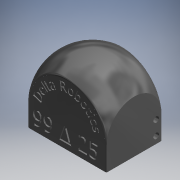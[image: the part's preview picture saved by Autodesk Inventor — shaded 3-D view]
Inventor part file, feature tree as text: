
AUTODESK INVENTOR PART (.ipt)
format: ipt  version: 2019 (Build 230136000, 136)  size: 742,912 bytes
history: native  units: mm (DEFAULTED — no unit token found)
features: sketch x11, extrude x10, plane x5, mirror x3, revolve x1, fillet x1
ambient origin geometry x8: Origin, YZ Plane, XZ Plane, XY Plane, X Axis, Y Axis, Z Axis, Center Point
bodies: Solid1 (feature_tree)
feature tree (31):
  extrude  "Extrusion1"  Depth=88.9mm
  extrude  "Extrusion2"  Depth=25.4mm
  extrude  "Extrusion3"  Depth=3.175mm TaperAngle=0.0deg
  plane  "Work Plane1"
  mirror  "Mirror1"
  plane  "Work Plane2"
  revolve  "Revolution1"  [1 undecoded]
  extrude  "Extrusion4"  Depth=44.45mm
  plane  "Work Plane3"
  mirror  "Mirror2"
  fillet  "Fillet1"  Radius=44.45mm
  sketch  "Sketch7"  dims[d14=180.0deg d15=25.4mm d16=0.0mm]
  extrude  "Extrusion5"  Depth=25.4mm TaperAngle=0.0deg
  extrude  "Extrusion6"  Depth=3.175mm
  plane  "Work Plane4"
  extrude  "Extrusion7"  Depth=8.001mm
  plane  "Work Plane5"
  mirror  "Mirror3"
  extrude  "Extrusion8"  Depth=6.35mm
  extrude  "Extrusion9"  Depth=3.048mm
  extrude  "Extrusion10"  Depth=3.175mm TaperAngle=0.0deg
  sketch  "Sketch1"  dims[d0=82.55mm d1=88.9mm]
  sketch  "Sketch2"  dims[d2=25.4mm d3=25.4mm]
  sketch  "Sketch3"  dims[d4=59.69mm d5=0.0mm d6=3.175mm d7=0.0mm]
  sketch  "Sketch5"  dims[d8=12.7mm d9=25.4mm]
  sketch  "Sketch6"  dims[d10=9.525mm d11=0.0mm d12=44.45mm d13=44.45mm]
  sketch  "Sketch8"  dims[d17=3.175mm d18=6.35mm]
  sketch  "Sketch9"  dims[d19=6.35mm d20=8.001mm]
  sketch  "Sketch10"  dims[d21=24.003mm d22=6.35mm]
  sketch  "Sketch11"  dims[d23=2.54mm d24=0.0mm d25=3.048mm]
  sketch  "Sketch12"  dims[d26=3.048mm d27=2.54mm d28=0.0mm d29=6.35mm d30=6.35mm d31=19.05mm d32=0.0mm d33=38.1mm d34=1.27mm d35=0.0mm d36=1.5875mm d37=0.0mm d38=3.175mm d39=3.175mm d40=3.175mm d41=19.05mm d42=12.7mm d43=12.7mm d44=12.7mm d45=85.725mm d46=0.0mm d47=25.4mm d48=0.0mm]
note: 1 required parameter value undecoded (feature->parameter linkage not recoverable at this tier; creation-order binding heuristic only, values carry confidence <= 0.55)
